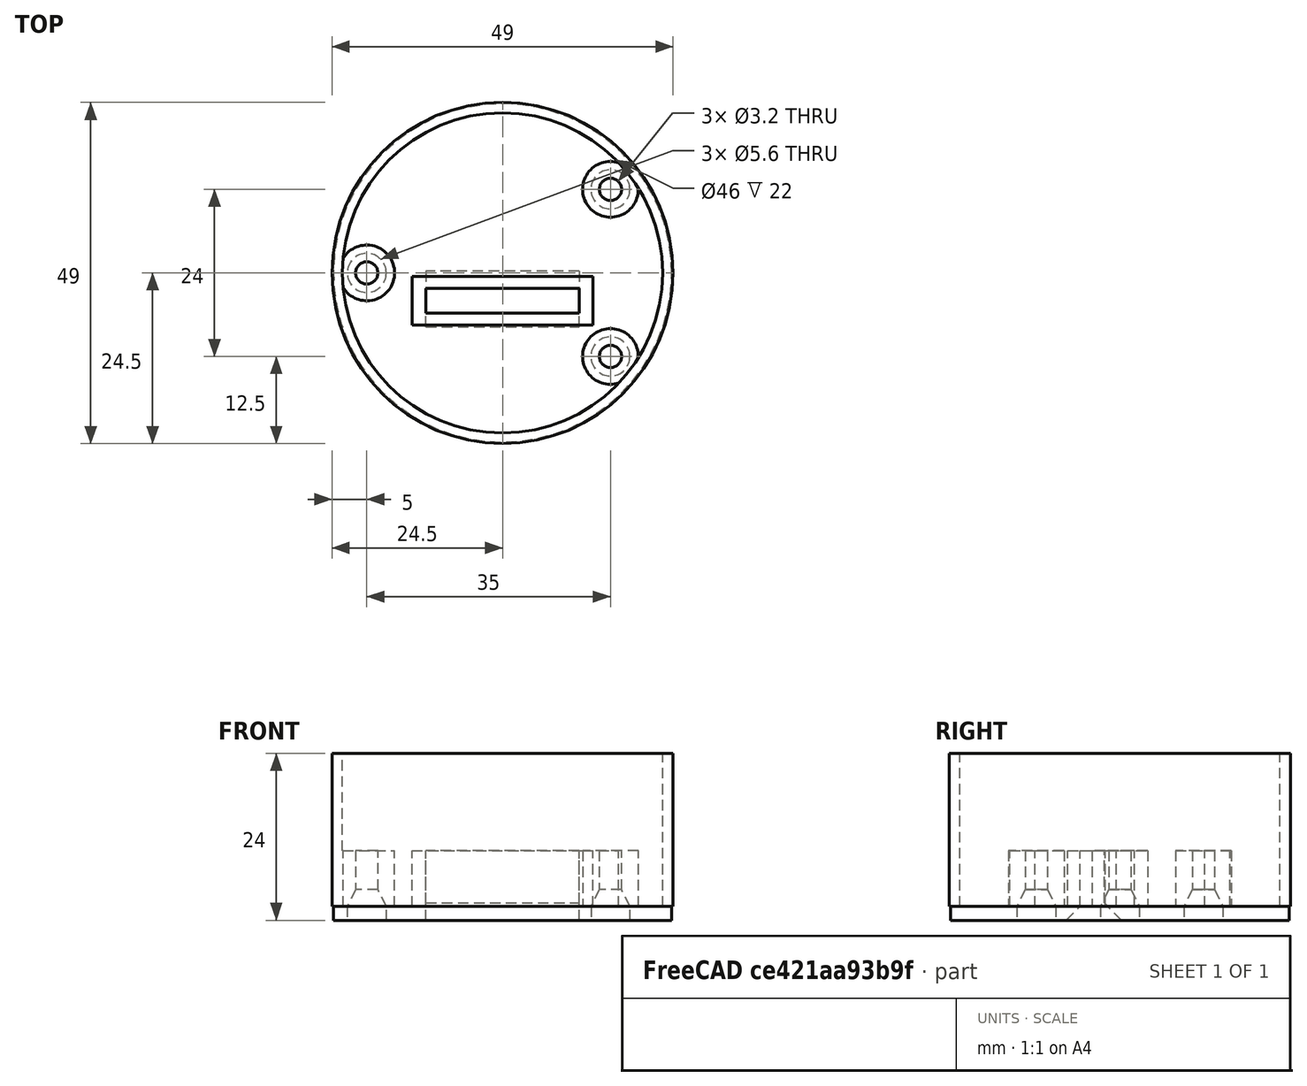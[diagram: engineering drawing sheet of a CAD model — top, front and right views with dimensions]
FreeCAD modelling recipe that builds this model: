
FCSTD DOCUMENT  (FreeCAD 0.21R33771 (Git))
Label: shell3
License: All rights reserved
LicenseURL: http://en.wikipedia.org/wiki/All_rights_reserved
objects: Part::Cut×11, Part::Cylinder×10, Part::MultiFuse×5, Part::Box×3, Part::Cone×3, Part::FeaturePython×1
note: 33 computed .brp shape members not serialized (recipe doc carries the construction recipe); baked Part::Feature solids carry a one-line shape summary decoded from their .brp

FEATURE [Part::Cylinder] Cylinder  label="円柱"
  Angle = 360
  AttacherType = Attacher::AttachEngine3D
  FirstAngle = 0
  Height = 2
  Radius = 24.3
  SecondAngle = 0
FEATURE [Part::FeaturePython] Tube  # WARN: FeaturePython — macro-defined, semantics opaque (R4)
  AttacherType = Attacher::AttachEngine3D
  Height = 22
  InnerRadius = 23
  OuterRadius = 24.5
  Placement = pos=(0,0,2) rot=(0,0,1;0rad)
FEATURE [Part::MultiFuse] Fusion
  Shapes = -> [Cylinder,Tube]
FEATURE [Part::Box] Box  label="立方体"
  AttacherType = Attacher::AttachEngine3D
  Height = 8
  Length = 26
  Placement = pos=(-13,-7.5,2) rot=(0,0,1;0rad)
  Width = 7
FEATURE [Part::MultiFuse] Fusion001
  Shapes = -> [Fusion,Box]
FEATURE [Part::Box] Box001  label="立方体001"
  AttacherType = Attacher::AttachEngine3D
  Height = 15
  Length = 22
  Placement = pos=(-11,-5.75,-1) rot=(0,0,1;0rad)
  Width = 3.5
FEATURE [Part::Cut] Cut
  Base = -> Fusion001
  Tool = -> Box001
FEATURE [Part::Cylinder] Cylinder010  label="円柱010"
  Angle = 360
  AttacherType = Attacher::AttachEngine3D
  FirstAngle = 0
  Height = 10
  Placement = pos=(15.5,-12,0) rot=(0,0,1;0rad)
  Radius = 1.6
  SecondAngle = 0
FEATURE [Part::Cone] Cone002  label="円錐002"
  Angle = 360
  AttacherType = Attacher::AttachEngine3D
  Height = 5.6
  Placement = pos=(15.5,-12,2) rot=(0,0,1;0rad)
  Radius1 = 2.8
  Radius2 = 0
FEATURE [Part::Cylinder] Cylinder009  label="円柱009"
  Angle = 360
  AttacherType = Attacher::AttachEngine3D
  FirstAngle = 0
  Height = 2
  Placement = pos=(15.5,-12,0) rot=(0,0,1;0rad)
  Radius = 2.8
  SecondAngle = 0
FEATURE [Part::Cylinder] Cylinder008  label="円柱008"
  Angle = 360
  AttacherType = Attacher::AttachEngine3D
  FirstAngle = 0
  Height = 8
  Placement = pos=(15.5,-12,2) rot=(0,0,1;0rad)
  Radius = 4
  SecondAngle = 0
FEATURE [Part::Cylinder] Cylinder007  label="円柱007"
  Angle = 360
  AttacherType = Attacher::AttachEngine3D
  FirstAngle = 0
  Height = 10
  Placement = pos=(15.5,12,0) rot=(0,0,1;0rad)
  Radius = 1.6
  SecondAngle = 0
FEATURE [Part::Cone] Cone001  label="円錐001"
  Angle = 360
  AttacherType = Attacher::AttachEngine3D
  Height = 5.6
  Placement = pos=(15.5,12,2) rot=(0,0,1;0rad)
  Radius1 = 2.8
  Radius2 = 0
FEATURE [Part::Cylinder] Cylinder006  label="円柱006"
  Angle = 360
  AttacherType = Attacher::AttachEngine3D
  FirstAngle = 0
  Height = 2
  Placement = pos=(15.5,12,0) rot=(0,0,1;0rad)
  Radius = 2.8
  SecondAngle = 0
FEATURE [Part::Cylinder] Cylinder005  label="円柱005"
  Angle = 360
  AttacherType = Attacher::AttachEngine3D
  FirstAngle = 0
  Height = 8
  Placement = pos=(15.5,12,2) rot=(0,0,1;0rad)
  Radius = 4
  SecondAngle = 0
FEATURE [Part::Cylinder] Cylinder004  label="円柱004"
  Angle = 360
  AttacherType = Attacher::AttachEngine3D
  FirstAngle = 0
  Height = 10
  Placement = pos=(-19.5,0,0) rot=(0,0,1;0rad)
  Radius = 1.6
  SecondAngle = 0
FEATURE [Part::Cone] Cone  label="円錐"
  Angle = 360
  AttacherType = Attacher::AttachEngine3D
  Height = 5.6
  Placement = pos=(-19.5,0,2) rot=(0,0,1;0rad)
  Radius1 = 2.8
  Radius2 = 0
FEATURE [Part::Cylinder] Cylinder003  label="円柱003"
  Angle = 360
  AttacherType = Attacher::AttachEngine3D
  FirstAngle = 0
  Height = 2
  Placement = pos=(-19.5,0,0) rot=(0,0,1;0rad)
  Radius = 2.8
  SecondAngle = 0
FEATURE [Part::Cylinder] Cylinder001  label="円柱001"
  Angle = 360
  AttacherType = Attacher::AttachEngine3D
  FirstAngle = 0
  Height = 8
  Placement = pos=(-19.5,0,2) rot=(0,0,1;0rad)
  Radius = 4
  SecondAngle = 0
FEATURE [Part::MultiFuse] Fusion002
  Shapes = -> [Cut,Cylinder001]
FEATURE [Part::Cut] Cut001
  Base = -> Fusion002
  Tool = -> Cylinder003
FEATURE [Part::Cut] Cut002
  Base = -> Cut001
  Tool = -> Cone
FEATURE [Part::Cut] Cut003
  Base = -> Cut002
  Tool = -> Cylinder004
FEATURE [Part::MultiFuse] Fusion003
  Shapes = -> [Cut003,Cylinder005]
FEATURE [Part::Cut] Cut004
  Base = -> Fusion003
  Tool = -> Cylinder006
FEATURE [Part::Cut] Cut005
  Base = -> Cut004
  Tool = -> Cone001
FEATURE [Part::Cut] Cut006
  Base = -> Cut005
  Tool = -> Cylinder007
FEATURE [Part::MultiFuse] Fusion004
  Shapes = -> [Cut006,Cylinder008]
FEATURE [Part::Cut] Cut007
  Base = -> Fusion004
  Tool = -> Cylinder009
FEATURE [Part::Cut] Cut008
  Base = -> Cut007
  Tool = -> Cone002
FEATURE [Part::Cut] Cut009
  Base = -> Cut008
  Tool = -> Cylinder010
FEATURE [Part::Box] Box002  label="立方体002"
  AttacherType = Attacher::AttachEngine3D
  Height = 10
  Length = 22
  Placement = pos=(-11,-3.75,-10.15) rot=(1,0,0;0.785398rad)
  Width = 10
FEATURE [Part::Cut] Cut010
  Base = -> Cut009
  Tool = -> Box002
